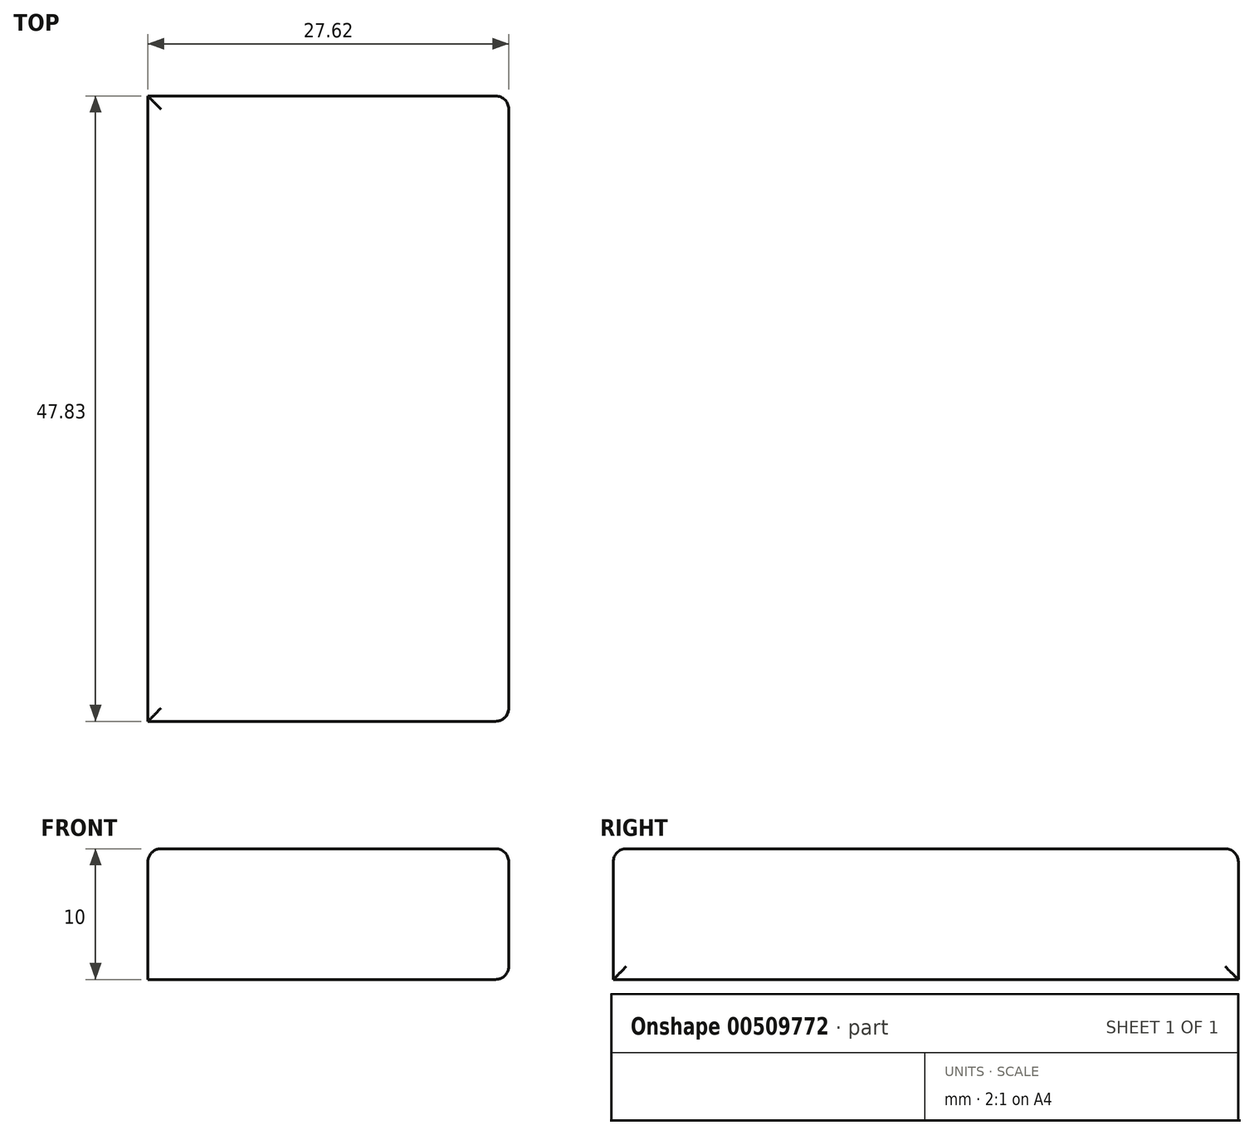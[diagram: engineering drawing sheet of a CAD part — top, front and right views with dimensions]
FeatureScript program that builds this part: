
annotation { "Feature Type Name" : "Feature", "Feature Type Description" : "" }
export const myFeature = defineFeature(function(context is Context, id is Id, definition is map)
    precondition{}
    {
        {
            var Q0;
            Q0=qCreatedBy(makeId("Top.planeOp"),FACE);
            var sketch = newSketch(context, id + "F0", { "sketchPlane" : qUnion([Q0])});
            skLineSegment(sketch, "E0.bottom", {"start": v(-35.87, 28.85) * mm, "end": v(-8.25, 28.85) * mm});
            skLineSegment(sketch, "E0.top", {"start": v(-35.87, -18.98) * mm, "end": v(-8.25, -18.98) * mm});
            skLineSegment(sketch, "E0.left", {"start": v(-35.87, 28.85) * mm, "end": v(-35.87, -18.98) * mm});
            skLineSegment(sketch, "E0.right", {"start": v(-8.25, 28.85) * mm, "end": v(-8.25, -18.98) * mm});
            skSolve(sketch);
        }
        {
            var Q0;
            Q0=makeQuery(id+"F0.imprint","IMPRINT",FACE,{"disambiguationData":[TD([[makeQuery(id+"F0.imprint","IMPRINT",EDGE,{"derivedFrom":sQuery(id+"F0.wireOp",EDGE,"E0.bottom")}),-1.0]])]});
            extrude(context, id + "F1", {"entities" : qUnion([Q0]), "depth" : 10 * mm, "offsetDistance" : 25 * mm});
        }
        {
            var Q0;
            Q0=makeQuery(id+"F1.opExtrude","SWEPT_FACE",FACE,{"disambiguationData":[OSD([sQuery(id+"F0.wireOp",EDGE,"E0.right")])]});
            var Q1;
            Q1=makeQuery(id+"F1.opExtrude","CAP_FACE",FACE,{"disambiguationData":[OSD([sQuery(id+"F0.wireOp",EDGE,"E0.bottom"),sQuery(id+"F0.wireOp",EDGE,"E0.top"),sQuery(id+"F0.wireOp",EDGE,"E0.left"),sQuery(id+"F0.wireOp",EDGE,"E0.right")])],"isStart":false});
            var Q2;
            Q2=makeQuery(id+"F1.opExtrude","SWEPT_EDGE",EDGE,{"disambiguationData":[OSD([sQuery(id+"F0.wireOp",EDGE,"E0.top"),sQuery(id+"F0.wireOp",EDGE,"E0.right")])]});
            fillet(context, id + "F2", {"entities" : qUnion([Q0, Q1, Q2]), "radius" : 1 * mm, "tangentPropagation" : true, "allowEdgeOverflow" : false});
        }
        {
            var Q0;
            Q0=makeQuery(id+"F1.opExtrude","CAP_FACE",FACE,{"disambiguationData":[OSD([sQuery(id+"F0.wireOp",EDGE,"E0.bottom"),sQuery(id+"F0.wireOp",EDGE,"E0.top"),sQuery(id+"F0.wireOp",EDGE,"E0.left"),sQuery(id+"F0.wireOp",EDGE,"E0.right")])],"isStart":false});
            var sketch = newSketch(context, id + "F3", { "sketchPlane" : qUnion([Q0])});
            skCircle(sketch, "E1", {"center": v(-21.66, 15.08) * mm, "radius": 2.77 * mm});
            skSolve(sketch);
        }
        {
            var Q0;
            Q0=sQuery(id+"F3.wireOp",EDGE,"E1");
            extrude(context, id + "F4", {"bodyType" : ToolBodyType.SURFACE, "surfaceEntities" : qUnion([Q0]), "depth" : -10 * mm, "offsetDistance" : 25 * mm});
        }
    });
